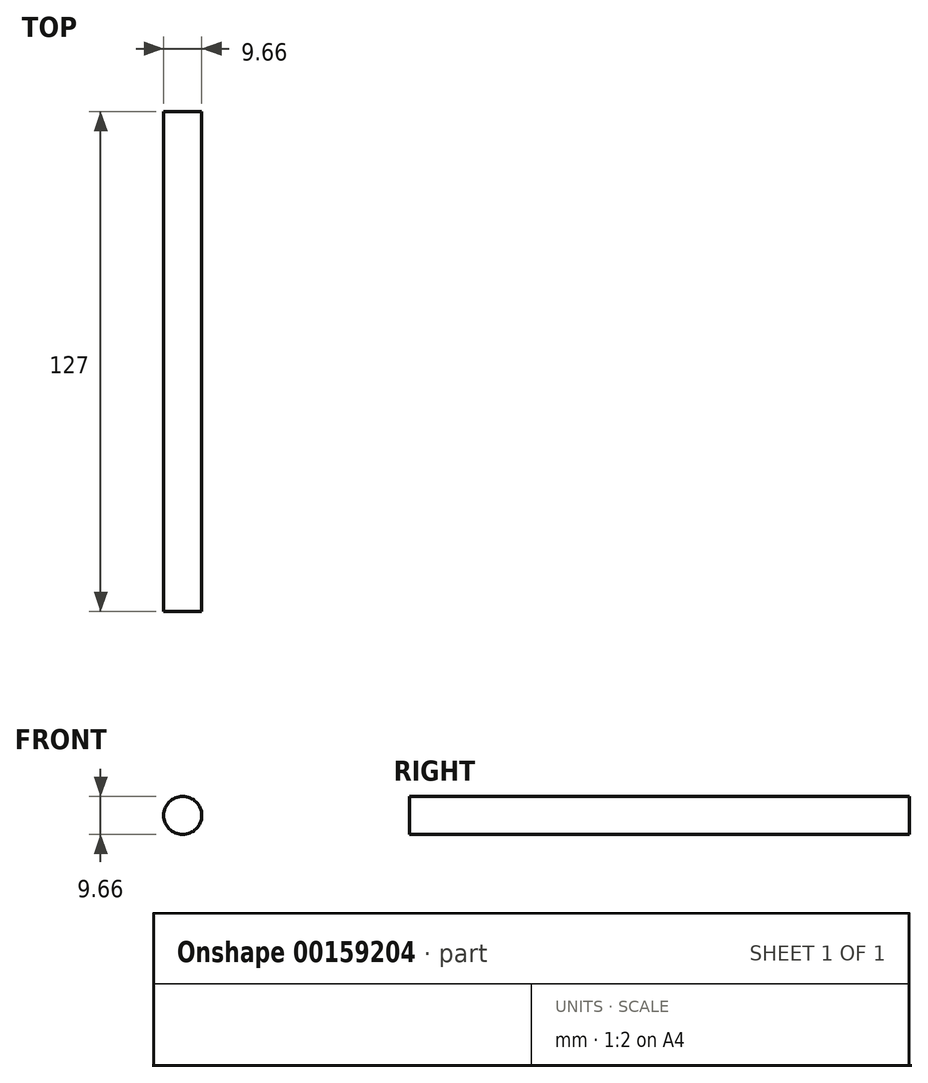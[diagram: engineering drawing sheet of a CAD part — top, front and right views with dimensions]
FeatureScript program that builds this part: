
annotation { "Feature Type Name" : "Feature", "Feature Type Description" : "" }
export const myFeature = defineFeature(function(context is Context, id is Id, definition is map)
    precondition{}
    {
        {
            var Q0;
            Q0=qCreatedBy(makeId("Front.planeOp"),FACE);
            var sketch = newSketch(context, id + "F0", { "sketchPlane" : qUnion([Q0])});
            skCircle(sketch, "E0", {"center": v(0, 0) * mm, "radius": 4.83 * mm});
            skSolve(sketch);
        }
        {
            var Q0;
            Q0 = qSketchRegion(id + "F0", true);
            extrude(context, id + "F1", {"entities" : qUnion([Q0]), "depth" : 127 * mm});
        }
    });
